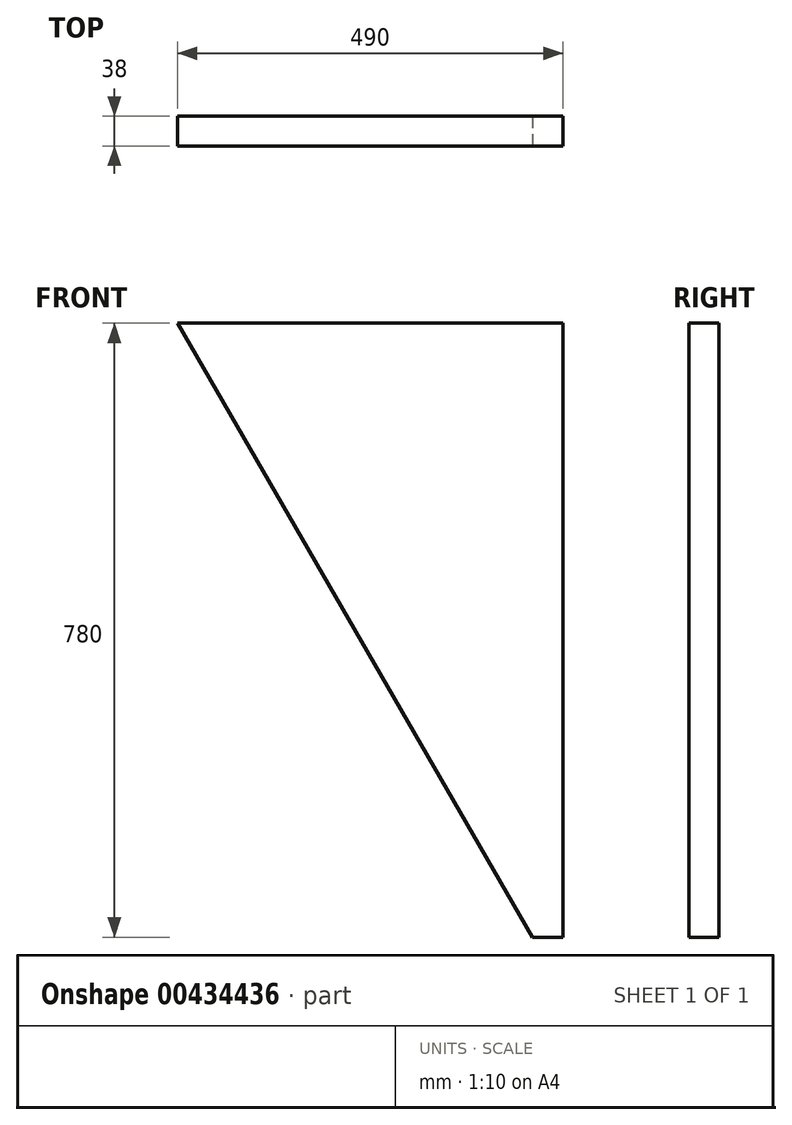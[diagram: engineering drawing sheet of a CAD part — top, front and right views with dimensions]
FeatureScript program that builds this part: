
annotation { "Feature Type Name" : "Feature", "Feature Type Description" : "" }
export const myFeature = defineFeature(function(context is Context, id is Id, definition is map)
    precondition{}
    {
        {
            var Q0;
            Q0=qCreatedBy(makeId("Front.planeOp"),FACE);
            var sketch = newSketch(context, id + "F0", { "sketchPlane" : qUnion([Q0])});
            skLineSegment(sketch, "E0.bottom", {"start": v(-245, 390) * mm, "end": v(245, 390) * mm});
            skLineSegment(sketch, "E0.top", {"start": v(-245, -390) * mm, "end": v(245, -390) * mm});
            skLineSegment(sketch, "E0.left", {"start": v(-245, 390) * mm, "end": v(-245, -390) * mm});
            skLineSegment(sketch, "E0.right", {"start": v(245, 390) * mm, "end": v(245, -390) * mm});
            skLineSegment(sketch, "E1", {"start": v(-245, 390) * mm, "end": v(245, -390) * mm, "construction": true});
            skSolve(sketch);
        }
        {
            var Q0;
            Q0=qSketchRegion(id+"F0",true);
            extrude(context, id + "F1", {"entities" : qUnion([Q0]), "endBound" : BoundingType.SYMMETRIC, "depth" : 38 * mm, "offsetDistance" : 25 * mm});
        }
        {
            var Q0;
            Q0=makeQuery(id+"F1.opExtrude","CAP_FACE",FACE,{"disambiguationData":[OSD([sQuery(id+"F0.wireOp",EDGE,"E0.bottom"),sQuery(id+"F0.wireOp",EDGE,"E0.top"),sQuery(id+"F0.wireOp",EDGE,"E0.left"),sQuery(id+"F0.wireOp",EDGE,"E0.right")])],"isStart":false});
            var sketch = newSketch(context, id + "F2", { "sketchPlane" : qUnion([Q0])});
            skLineSegment(sketch, "E2", {"start": v(-245, 390) * mm, "end": v(206, -390) * mm});
            skLineSegment(sketch, "E3", {"start": v(206, -390) * mm, "end": v(-245, -390) * mm});
            skLineSegment(sketch, "E4", {"start": v(-245, -390) * mm, "end": v(-245, 390) * mm});
            skSolve(sketch);
        }
        {
            var Q0;
            Q0 = qSketchRegion(id + "F2", true);
            extrude(context, id + "F3", {"entities" : qUnion([Q0]), "operationType" : NewBodyOperationType.REMOVE, "endBound" : BoundingType.THROUGH_ALL, "oppositeDirection" : true, "depth" : 25 * mm});
        }
    });
